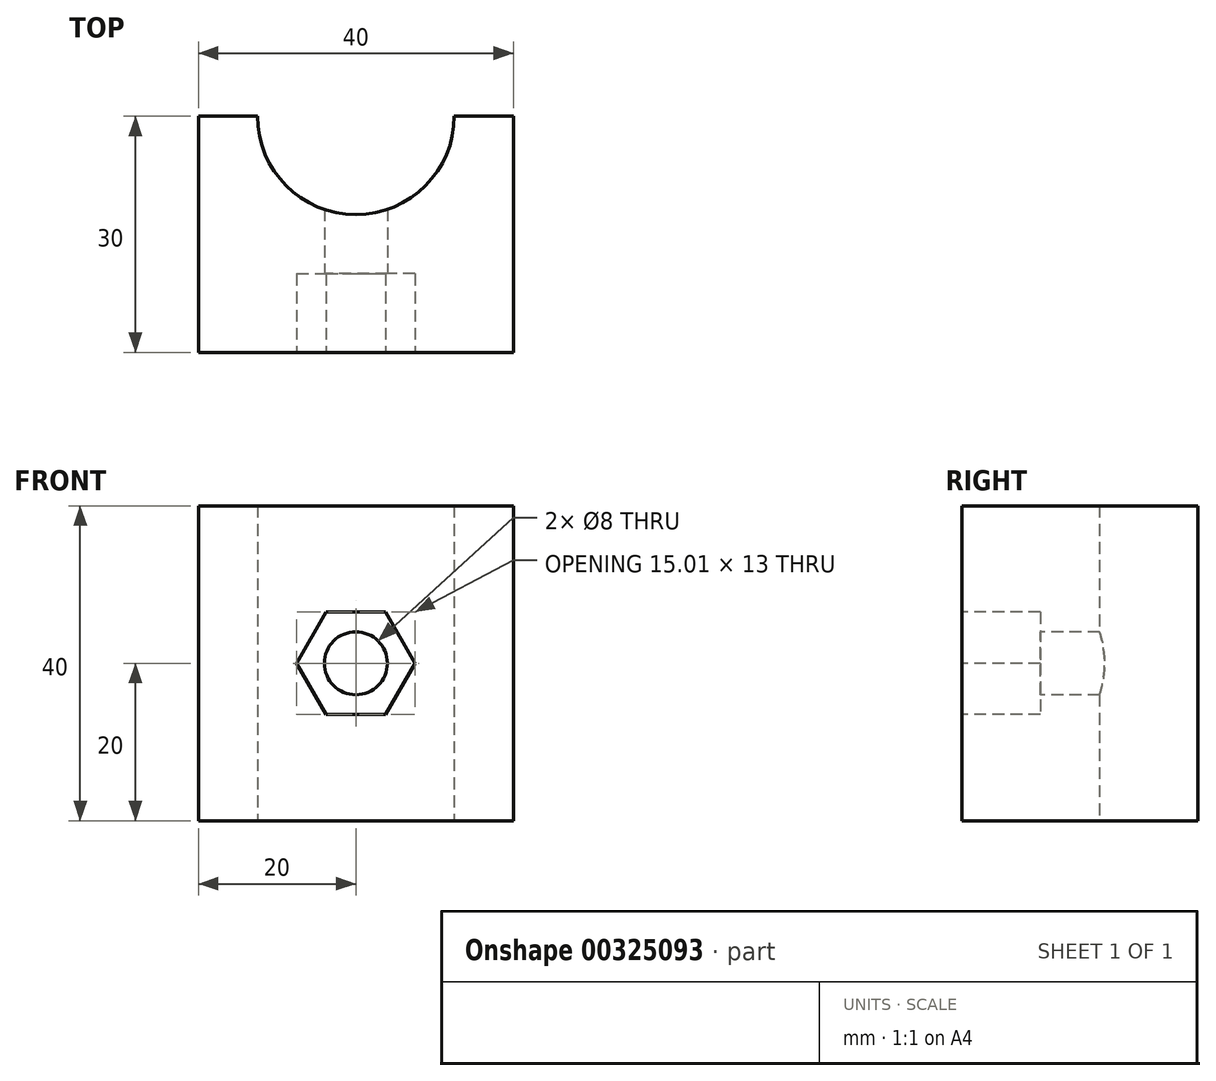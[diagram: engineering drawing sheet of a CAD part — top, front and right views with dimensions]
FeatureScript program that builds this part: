
annotation { "Feature Type Name" : "Feature", "Feature Type Description" : "" }
export const myFeature = defineFeature(function(context is Context, id is Id, definition is map)
    precondition{}
    {
        {
            var Q0;
            Q0=qCreatedBy(makeId("Top.planeOp"),FACE);
            var sketch = newSketch(context, id + "F0", { "sketchPlane" : qUnion([Q0])});
            skLineSegment(sketch, "E0.bottom", {"start": v(20, -15) * mm, "end": v(-20, -15) * mm});
            skLineSegment(sketch, "E0.top", {"start": v(20, 15) * mm, "end": v(12.5, 15) * mm});
            skLineSegment(sketch, "E0.left", {"start": v(20, -15) * mm, "end": v(20, 15) * mm});
            skLineSegment(sketch, "E0.right", {"start": v(-20, -15) * mm, "end": v(-20, 15) * mm});
            skPoint(sketch, "E0.middle", {"position": v(0, 0) * mm});
            skLineSegment(sketch, "E1", {"start": v(-12.5, 15) * mm, "end": v(-20, 15) * mm});
            skPoint(sketch, "E2", {"position": v(0, 2.5) * mm});
            skArc(sketch, "E3", {"start": v(-12.5, 15) * mm, "mid": v(0, 2.5) * mm, "end": v(12.5, 15) * mm});
            skSolve(sketch);
        }
        {
            var Q0;
            Q0=makeQuery(id+"F0.imprint","IMPRINT",FACE,{"disambiguationData":[TD([[makeQuery(id+"F0.imprint","IMPRINT",EDGE,{"derivedFrom":sQuery(id+"F0.wireOp",EDGE,"E0.bottom")}),-1.0]])]});
            extrude(context, id + "F1", {"entities" : qUnion([Q0]), "depth" : 40 * mm});
        }
        {
            var Q0;
            Q0=makeQuery(id+"F1.opExtrude","SWEPT_FACE",FACE,{"disambiguationData":[OSD([sQuery(id+"F0.wireOp",EDGE,"E0.bottom")])]});
            var sketch = newSketch(context, id + "F2", { "sketchPlane" : qUnion([Q0])});
            skLineSegment(sketch, "E4", {"start": v(-20, 20) * mm, "end": v(20, 20) * mm});
            skLineSegment(sketch, "E5", {"start": v(0, 40) * mm, "end": v(0, 0) * mm});
            skPoint(sketch, "E6", {"position": v(0, 20) * mm});
            skCircle(sketch, "E7.cCircle", {"center": v(0, 20) * mm, "radius": 6.5 * mm, "construction": true});
            skLineSegment(sketch, "E7.0", {"start": v(-3.75, 26.5) * mm, "end": v(3.75, 26.5) * mm});
            skLineSegment(sketch, "E7.1", {"start": v(3.75, 26.5) * mm, "end": v(7.5, 20) * mm});
            skLineSegment(sketch, "E7.2", {"start": v(7.5, 20) * mm, "end": v(3.75, 13.5) * mm});
            skLineSegment(sketch, "E7.3", {"start": v(3.75, 13.5) * mm, "end": v(-3.75, 13.5) * mm});
            skLineSegment(sketch, "E7.4", {"start": v(-3.75, 13.5) * mm, "end": v(-7.5, 20) * mm});
            skLineSegment(sketch, "E7.5", {"start": v(-7.5, 20) * mm, "end": v(-3.75, 26.5) * mm});
            skPoint(sketch, "E7.0.midPoint", {"position": v(0, 26.5) * mm});
            skCircle(sketch, "E8", {"center": v(0, 20) * mm, "radius": 4 * mm});
            skSolve(sketch);
        }
        {
            var Q0;
            {var subQ0=sQuery(id+"F2.wireOp",EDGE,"E8");var subQ1=sQuery(id+"F2.wireOp",EDGE,"E4");var subQ2=makeQuery(id+"F2.imprint","INTERSECT",VERTEX,{"disambiguationData":[OD(0.0)],"derivedFrom":[subQ1,subQ0]});Q0=makeQuery(id+"F2.imprint","IMPRINT",FACE,{"disambiguationData":[TD([[makeQuery(id+"F2.imprint","IMPRINT",EDGE,{"disambiguationData":[TD([[subQ2,-1.0]])],"derivedFrom":subQ1}),-1.0]])]});}
            var Q1;
            {var subQ0=sQuery(id+"F2.wireOp",EDGE,"E5");var subQ1=sQuery(id+"F2.wireOp",EDGE,"E4");var subQ2=makeQuery(id+"F2.imprint","INTERSECT",VERTEX,{"derivedFrom":[subQ1,subQ0]});Q1=makeQuery(id+"F2.imprint","IMPRINT",FACE,{"disambiguationData":[TD([[makeQuery(id+"F2.imprint","IMPRINT",EDGE,{"disambiguationData":[TD([[subQ2,-1.0]])],"derivedFrom":subQ1}),-1.0]])]});}
            var Q2;
            {var subQ0=sQuery(id+"F2.wireOp",EDGE,"E5");var subQ1=sQuery(id+"F2.wireOp",EDGE,"E4");var subQ2=makeQuery(id+"F2.imprint","INTERSECT",VERTEX,{"derivedFrom":[subQ1,subQ0]});Q2=makeQuery(id+"F2.imprint","IMPRINT",FACE,{"disambiguationData":[TD([[makeQuery(id+"F2.imprint","IMPRINT",EDGE,{"disambiguationData":[TD([[subQ2,-1.0]])],"derivedFrom":subQ1}),1.0]])]});}
            var Q3;
            {var subQ0=sQuery(id+"F2.wireOp",EDGE,"E8");var subQ1=sQuery(id+"F2.wireOp",EDGE,"E4");var subQ2=makeQuery(id+"F2.imprint","INTERSECT",VERTEX,{"disambiguationData":[OD(0.0)],"derivedFrom":[subQ1,subQ0]});Q3=makeQuery(id+"F2.imprint","IMPRINT",FACE,{"disambiguationData":[TD([[makeQuery(id+"F2.imprint","IMPRINT",EDGE,{"disambiguationData":[TD([[subQ2,-1.0]])],"derivedFrom":subQ1}),1.0]])]});}
            extrude(context, id + "F3", {"entities" : qUnion([Q0, Q1, Q2, Q3]), "operationType" : NewBodyOperationType.REMOVE, "endBound" : BoundingType.THROUGH_ALL, "oppositeDirection" : true, "depth" : 25 * mm});
        }
        {
            var Q0;
            {var subQ1=sQuery(id+"F2.wireOp",EDGE,"E7.2");Q0=makeQuery(id+"F2.imprint","IMPRINT",FACE,{"disambiguationData":[TD([[makeQuery(id+"F2.imprint","IMPRINT",EDGE,{"derivedFrom":subQ1}),-1.0]])]});}
            var Q1;
            {var subQ0=sQuery(id+"F2.wireOp",EDGE,"E7.1");Q1=makeQuery(id+"F2.imprint","IMPRINT",FACE,{"disambiguationData":[TD([[makeQuery(id+"F2.imprint","IMPRINT",EDGE,{"derivedFrom":subQ0}),-1.0]])]});}
            var Q2;
            {var subQ0=sQuery(id+"F2.wireOp",EDGE,"E7.5");Q2=makeQuery(id+"F2.imprint","IMPRINT",FACE,{"disambiguationData":[TD([[makeQuery(id+"F2.imprint","IMPRINT",EDGE,{"derivedFrom":subQ0}),-1.0]])]});}
            var Q3;
            {var subQ0=sQuery(id+"F2.wireOp",EDGE,"E7.4");Q3=makeQuery(id+"F2.imprint","IMPRINT",FACE,{"disambiguationData":[TD([[makeQuery(id+"F2.imprint","IMPRINT",EDGE,{"derivedFrom":subQ0}),-1.0]])]});}
            extrude(context, id + "F4", {"entities" : qUnion([Q0, Q1, Q2, Q3]), "operationType" : NewBodyOperationType.REMOVE, "oppositeDirection" : true, "depth" : 10 * mm});
        }
        {
            var Q0;
            Q0=makeQuery(id+"F1.opExtrude","SWEPT_BODY",BODY,{"disambiguationData":[OSD([sQuery(id+"F0.wireOp",EDGE,"E0.bottom"),sQuery(id+"F0.wireOp",EDGE,"E0.top"),sQuery(id+"F0.wireOp",EDGE,"E0.left"),sQuery(id+"F0.wireOp",EDGE,"E0.right"),sQuery(id+"F0.wireOp",EDGE,"E1"),sQuery(id+"F0.wireOp",EDGE,"E3")])]});
            transform(context, id + "F5", {"entities" : qUnion([Q0]), "transformType" : TransformType.TRANSLATION_3D, "dx" : 0 * mm, "dy" : 0 * mm, "dz" : 0 * mm, "makeCopy" : true});
        }
    });
